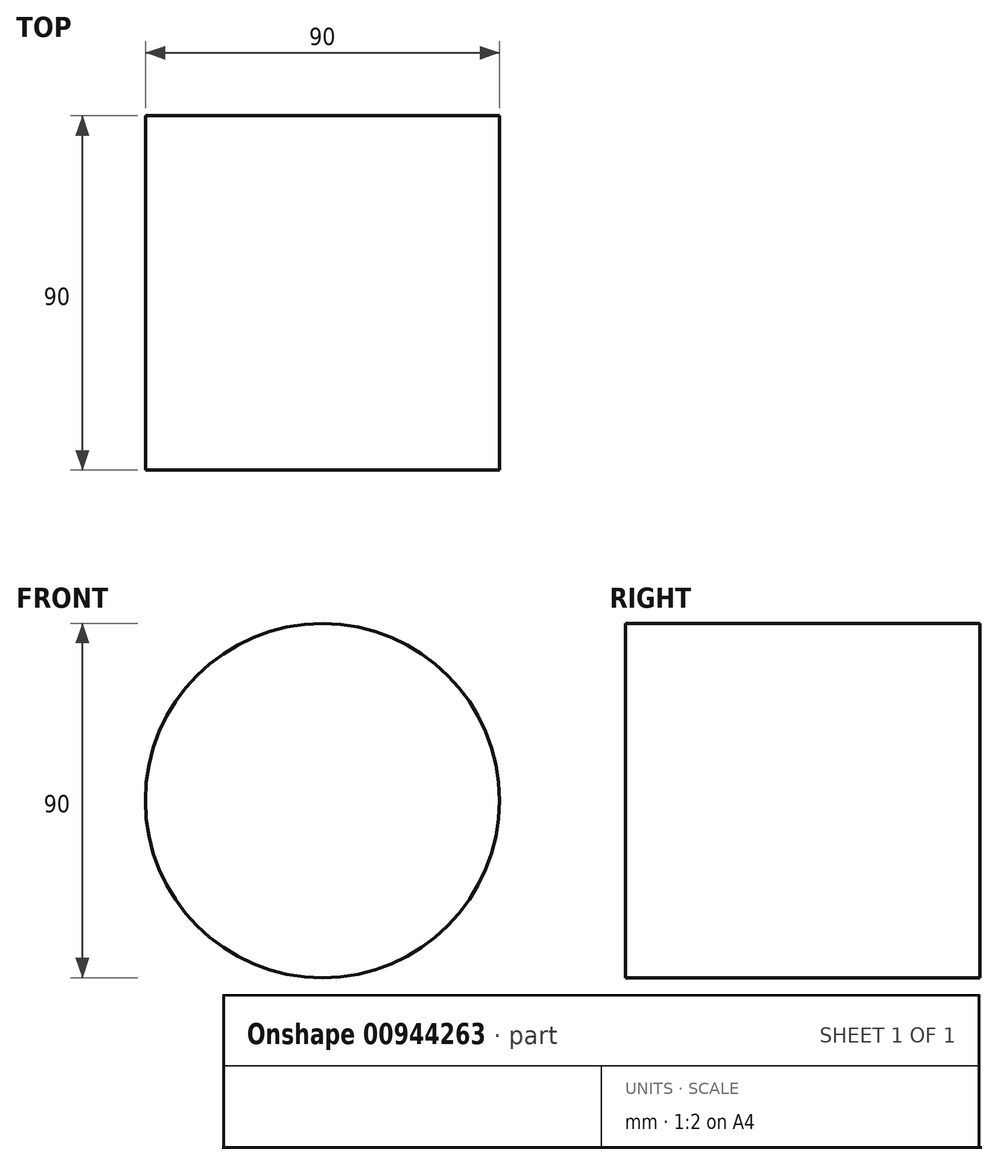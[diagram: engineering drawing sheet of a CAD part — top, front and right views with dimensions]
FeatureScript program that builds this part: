
annotation { "Feature Type Name" : "Feature", "Feature Type Description" : "" }
export const myFeature = defineFeature(function(context is Context, id is Id, definition is map)
    precondition{}
    {
        {
            var Q0;
            Q0=qCreatedBy(makeId("Front.planeOp"),FACE);
            var sketch = newSketch(context, id + "F0", { "sketchPlane" : qUnion([Q0])});
            skCircle(sketch, "E0", {"center": v(0, 0) * mm, "radius": 45 * mm});
            skSolve(sketch);
        }
        {
            var Q0;
            Q0 = qSketchRegion(id + "F0", true);
            extrude(context, id + "F1", {"entities" : qUnion([Q0]), "depth" : 90 * mm, "offsetDistance" : 25 * mm});
        }
    });
